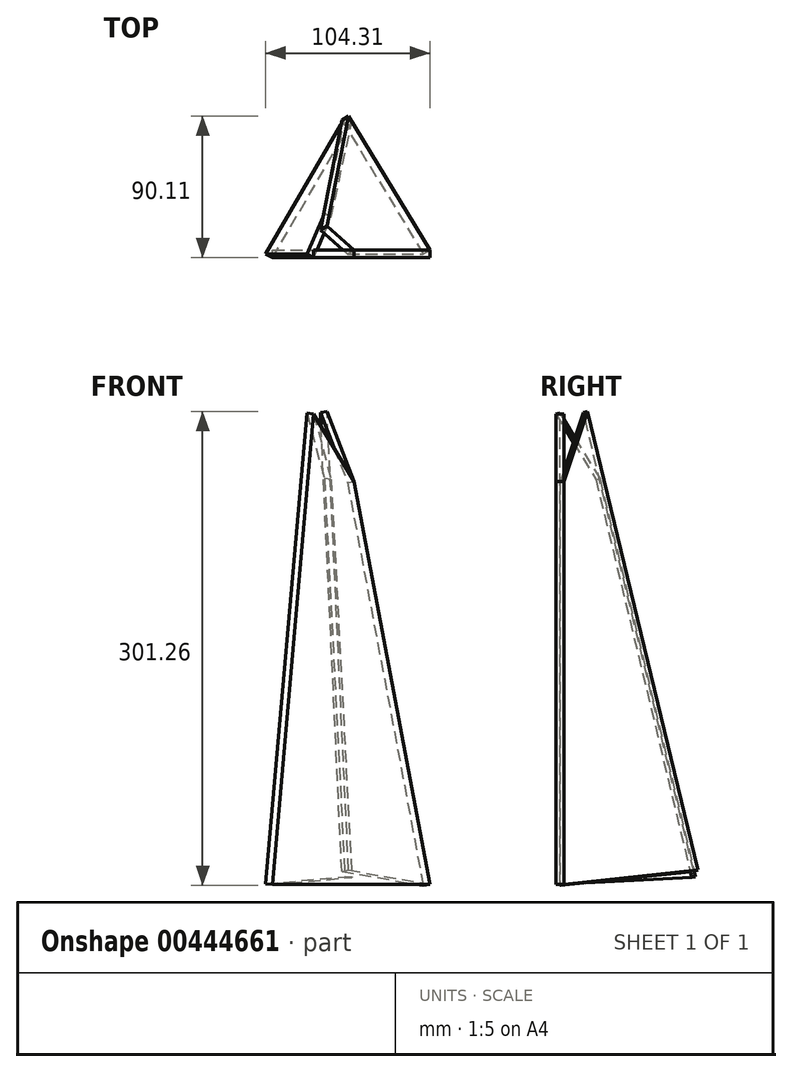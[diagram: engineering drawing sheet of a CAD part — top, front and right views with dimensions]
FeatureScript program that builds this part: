
annotation { "Feature Type Name" : "Feature", "Feature Type Description" : "" }
export const myFeature = defineFeature(function(context is Context, id is Id, definition is map)
    precondition{}
    {
        {
            var Q0;
            Q0=qCreatedBy(makeId("Front.planeOp"),FACE);
            var sketch = newSketch(context, id + "F0", { "sketchPlane" : qUnion([Q0])});
            skLineSegment(sketch, "E0", {"start": v(-112.34, -36.6) * mm, "end": v(-12.34, -36.6) * mm});
            skLineSegment(sketch, "E1", {"start": v(-112.34, -36.6) * mm, "end": v(-86.2, 262.26) * mm});
            skLineSegment(sketch, "E2", {"start": v(-86.2, 262.26) * mm, "end": v(-60.44, 219.4) * mm});
            skLineSegment(sketch, "E3", {"start": v(-60.44, 219.4) * mm, "end": v(-12.34, -36.6) * mm});
            skSolve(sketch);
        }
        {
            var Q0;
            Q0=makeQuery(id+"F0.imprint","IMPRINT",FACE,{"disambiguationData":[TD([[makeQuery(id+"F0.imprint","IMPRINT",EDGE,{"derivedFrom":sQuery(id+"F0.wireOp",EDGE,"E0")}),1.0]])]});
            extrude(context, id + "F1", {"entities" : qUnion([Q0]), "depth" : 5 * mm});
        }
        {
            var Q0;
            Q0=makeQuery(id+"F1.opExtrude","SWEPT_BODY",BODY,{"disambiguationData":[OSD([sQuery(id+"F0.wireOp",EDGE,"E0"),sQuery(id+"F0.wireOp",EDGE,"E1"),sQuery(id+"F0.wireOp",EDGE,"E2"),sQuery(id+"F0.wireOp",EDGE,"E3")])]});
            var Q1;
            Q1=makeQuery(id+"F1.opExtrude","CAP_EDGE",EDGE,{"disambiguationData":[OSD([sQuery(id+"F0.wireOp",EDGE,"E3")])],"isStart":true});
            transform(context, id + "F2", {"entities" : qUnion([Q0]), "transformType" : TransformType.ROTATION, "transformAxis" : qUnion([Q1]), "angle" : 60 * degree, "makeCopy" : true});
        }
        {
            var Q0;
            Q0=makeQuery(id+"F1.opExtrude","SWEPT_BODY",BODY,{"disambiguationData":[OSD([sQuery(id+"F0.wireOp",EDGE,"E0"),sQuery(id+"F0.wireOp",EDGE,"E1"),sQuery(id+"F0.wireOp",EDGE,"E2"),sQuery(id+"F0.wireOp",EDGE,"E3")])]});
            var Q1;
            Q1=makeQuery(id+"F1.opExtrude","CAP_EDGE",EDGE,{"disambiguationData":[OSD([sQuery(id+"F0.wireOp",EDGE,"E1")])],"isStart":false});
            transform(context, id + "F3", {"entities" : qUnion([Q0]), "transformType" : TransformType.ROTATION, "transformAxis" : qUnion([Q1]), "angle" : 60 * degree, "makeCopy" : true});
        }
    });
